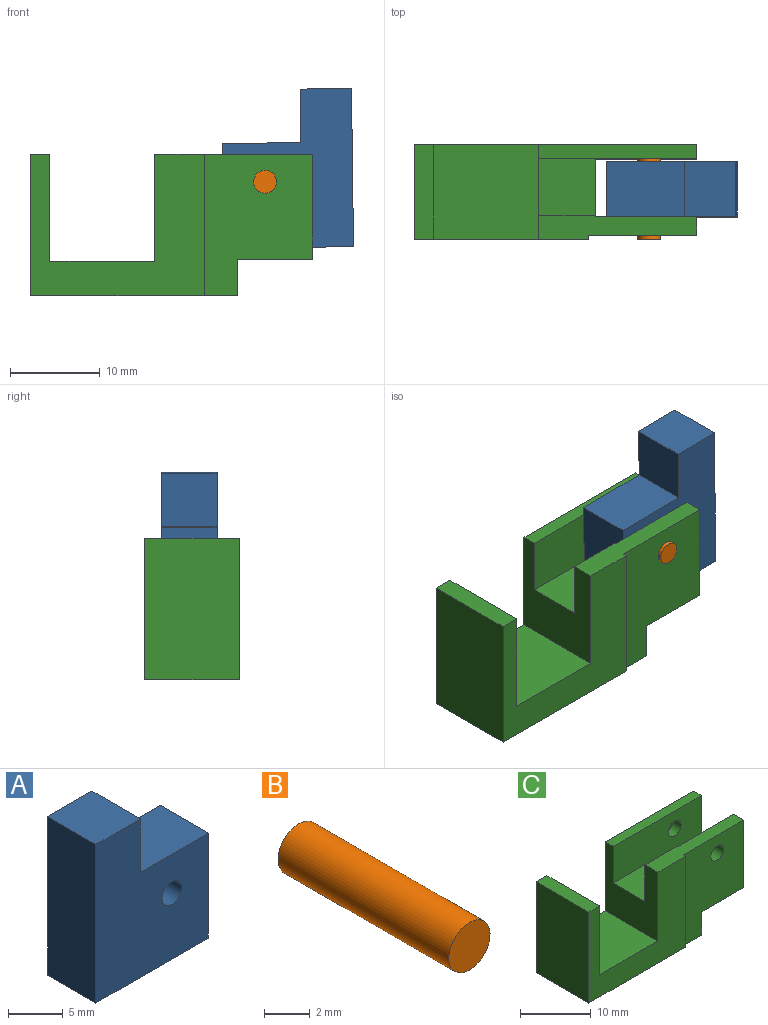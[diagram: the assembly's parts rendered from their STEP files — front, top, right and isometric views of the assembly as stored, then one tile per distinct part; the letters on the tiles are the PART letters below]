
ASSEMBLY  parts=3 mates=2
PART A: 9 faces, bbox 14.5x6.2x17.7 mm
  f0: plane 11.68x6.22mm, normal (1,0,0), area 72.7mm2, adj f1,f2,f5,f6
  f1: plane 17.65x14.48mm, normal (0,-1,0), area 198.3mm2, adj f0,f3,f4,f5,f6,f7,f8
  f2: plane 17.65x14.48mm, normal (0,1,0), area 198.3mm2, adj f0,f3,f4,f5,f6,f7,f8
  f3: plane 6.22x5.72mm, normal (0,0,1), area 35.6mm2, adj f1,f2,f4,f7
  f4: plane 17.65x6.22mm, normal (-1,0,0), area 109.9mm2, adj f1,f2,f3,f5
  f5: plane 14.48x6.22mm, normal (0,0,-1), area 90.1mm2, adj f0,f1,f2,f4
  f6: plane 8.76x6.22mm, normal (0,0,1), area 54.5mm2, adj f0,f1,f2,f7
  f7: plane 6.22x5.97mm, normal (1,0,0), area 37.1mm2, adj f1,f2,f3,f6
  f8: cylinder r=1.26mm len=6.22mm, axis (0,-1,0), area 49.2mm2, adj f1,f2
PART B: 3 faces, bbox 2.5x10.5x2.5 mm
  f0: cylinder r=1.27mm len=10.54mm, axis (0,1,0), area 84.2mm2, adj f1,f2
  f1: plane 2.54x2.54mm, normal (0,-1,0), area 5.1mm2, adj f0
  f2: plane 2.54x2.54mm, normal (0,1,0), area 5.1mm2, adj f0
PART C: 25 faces, bbox 31.5x10.5x15.7 mm
  f0: plane 17.65x2.59mm, normal (0,0,1), area 39mm2, adj f1,f2,f3,f5,f9,f14,f16,f21
  f1: plane 15.75x6.48mm, normal (1,0,0), area 61.6mm2, adj f0,f4,f14,f15,f21,f22
  f2: plane 11.94x10.54mm, normal (-1,0,0), area 85.5mm2, adj f0,f6,f7,f9,f13,f15,f21,f22
  f3: plane 15.75x12.09mm, normal (0,-1,0), area 151.3mm2, adj f0,f4,f5,f16,f19,f20,f24
  f4: plane 23.11x10.54mm, normal (0,0,-1), area 223mm2, adj f1,f3,f7,f8,f9,f14,f15,f16
  f5: plane 11.68x2.02mm, normal (1,0,0), area 23.6mm2, adj f0,f3,f14,f19
  f6: plane 17.65x1.59mm, normal (0,0,1), area 28mm2, adj f2,f7,f10,f15
  f7: plane 31.5x15.75mm, normal (0,1,0), area 317.5mm2, adj f2,f4,f6,f8,f10,f11,f12,f13
  f8: plane 15.75x10.54mm, normal (-1,0,0), area 166mm2, adj f4,f7,f9,f11
  f9: plane 19.41x15.75mm, normal (0,-1,0), area 166.2mm2, adj f0,f2,f4,f8,f11,f12,f13,f16
  f10: plane 11.68x1.59mm, normal (1,0,0), area 18.5mm2, adj f6,f7,f15,f18
  f11: plane 10.54x2.16mm, normal (0,0,1), area 22.8mm2, adj f7,f8,f9,f12
  f12: plane 11.94x10.54mm, normal (1,0,0), area 125.8mm2, adj f7,f9,f11,f13
  f13: plane 11.68x10.54mm, normal (0,0,1), area 123.2mm2, adj f2,f7,f9,f12
  f14: plane 15.75x11.3mm, normal (0,1,0), area 139mm2, adj f0,f1,f4,f5,f19,f20,f24
  f15: plane 17.65x15.75mm, normal (0,-1,0), area 179.3mm2, adj f1,f2,f4,f6,f10,f17,f18,f22
  f16: plane 15.75x0.45mm, normal (1,0,0), area 7.2mm2, adj f0,f3,f4,f9
  f17: plane 4.06x1.59mm, normal (1,0,0), area 6.5mm2, adj f4,f7,f15,f18
  f18: plane 8.38x1.59mm, normal (0,0,-1), area 13.3mm2, adj f7,f10,f15,f17
  f19: plane 8.38x2.02mm, normal (0,0,-1), area 17mm2, adj f3,f5,f14,f20
  f20: plane 4.06x2.02mm, normal (1,0,0), area 8.2mm2, adj f3,f4,f14,f19
  f21: plane 6.35x6.35mm, normal (0,1,0), area 40.3mm2, adj f0,f1,f2,f22
  f22: plane 6.36x6.35mm, normal (0,0,1), area 40.4mm2, adj f1,f2,f15,f21
  f23: cylinder r=1.26mm len=2.51mm, axis (0,-1,0), area 12.5mm2, adj f7,f15
  f24: cylinder r=1.26mm len=2.51mm, axis (0,-1,0), area 16mm2, adj f3,f14
PLACE A rot(axis=(0.01,0,-1),180deg) t=(69.82,3.06,-23.72)mm
PLACE B rot(axis=(-0.19,-0.96,-0.21),0deg) t=(97.24,11.12,-37.17)mm
PLACE C rot(axis=(-0.19,-0.96,-0.21),0deg) t=(60.16,11.94,-34.3)mm fixed
MATE revolute B.f0 <-> C.f23  axis (0,1,0) through (66.59,11.12,-21.6)mm
MATE revolute C.f23 <-> A.f8  axis (0,1,0) through (66.59,3.06,-21.6)mm
